# Revit family: E-917
name_source: partatom
category: Plumbing Fixtures
revit_build: Autodesk Revit 2014 (Build: 20130308_1515(x64)
units: mm (PartAtom-declared; Revit-internal decimal feet)

## types (1)
- E-917
    Accessories = Drain Push; Setting Kit Included; Key To Aerator; Cartridge Wrench; Insert Washbasin Without Overflow; Flexible Hoses
    Brass Chromed = Brass
    Data Sheet = http://helvex.com
    Description = Clásica Single Handle Lavatory With Drain Push
    Features = Single-Lever Sink Drain And Aerator Push Hidden
    Installation Thread = ½" - 14 NPSM
    Instructive = http://helvex.com
    Manufacturer = HELVEX
    Max. Working Pressure = 85.3 psi
    Min. Working Pressure = 5.7 psi
    Model = E-917
    Operation = The Handle Has A Horizontal Rotation Function Of Hot And Cold Water, And Vertically To Open And Close The Flow Of Water
    Support Base Diameter = 2"
    Total Depth = 8"
    Total Height = 7"
    Type Comments = Single Control Lavatory Faucet
    URL = http://helvex.com

## geometry (parser evidence)
native form markers: Sweep x3
no freeform markers — native parametric forms only
